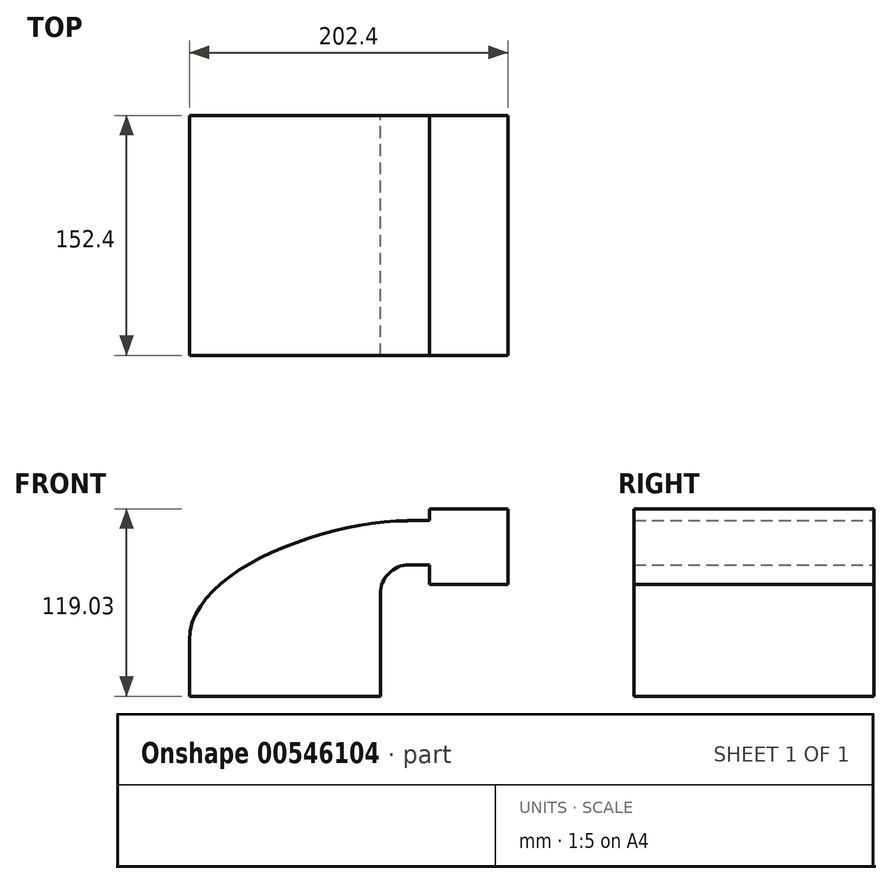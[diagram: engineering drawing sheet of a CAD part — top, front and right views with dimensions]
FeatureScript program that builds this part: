
annotation { "Feature Type Name" : "Feature", "Feature Type Description" : "" }
export const myFeature = defineFeature(function(context is Context, id is Id, definition is map)
    precondition{}
    {
        {
            var Q0;
            Q0=qCreatedBy(makeId("Front.planeOp"),FACE);
            var sketch = newSketch(context, id + "F0", { "sketchPlane" : qUnion([Q0])});
            skLineSegment(sketch, "E0.bottom", {"start": v(-60.63, 17.83) * mm, "end": v(60.63, 17.83) * mm});
            skLineSegment(sketch, "E0.top", {"start": v(-60.63, -17.83) * mm, "end": v(60.63, -17.83) * mm});
            skLineSegment(sketch, "E0.left", {"start": v(-60.63, 17.83) * mm, "end": v(-60.63, -17.83) * mm});
            skLineSegment(sketch, "E0.right", {"start": v(60.63, 17.83) * mm, "end": v(60.63, -17.83) * mm});
            skPoint(sketch, "E0.middle", {"position": v(0, 0) * mm});
            skLineSegment(sketch, "E1.bottom", {"start": v(141.77, 53.05) * mm, "end": v(91.84, 53.05) * mm});
            skLineSegment(sketch, "E1.top", {"start": v(141.77, 101.2) * mm, "end": v(91.84, 101.2) * mm});
            skLineSegment(sketch, "E1.left", {"start": v(141.77, 53.05) * mm, "end": v(141.77, 101.2) * mm});
            skLineSegment(sketch, "E1.right", {"start": v(91.84, 53.05) * mm, "end": v(91.84, 101.2) * mm});
            skPoint(sketch, "E1.middle", {"position": v(116.8, 77.13) * mm});
            skLineSegment(sketch, "E2", {"start": v(60.63, 17.83) * mm, "end": v(60.63, 47.26) * mm});
            skArc(sketch, "E3", {"start": v(60.63, 47.26) * mm, "mid": v(65.99, 60.19) * mm, "end": v(78.92, 65.54) * mm});
            skLineSegment(sketch, "E4", {"start": v(78.92, 65.54) * mm, "end": v(115.89, 65.54) * mm});
            skLineSegment(sketch, "E5.0", {"start": v(78.92, 93.63) * mm, "end": v(115.89, 93.63) * mm});
            skArc(sketch, "E5.1", {"start": v(32.55, 47.26) * mm, "mid": v(46.13, 80.05) * mm, "end": v(78.92, 93.63) * mm});
            skLineSegment(sketch, "E5.2", {"start": v(32.55, 17.83) * mm, "end": v(32.55, 47.26) * mm});
            skLineSegment(sketch, "E6", {"start": v(116.8, 53.05) * mm, "end": v(115.89, 101.2) * mm});
            skFitSpline(sketch, "E7", {"points": [v(-60.63, 17.83) * mm, v(78.92, 93.63) * mm], "startDerivative": vector(0, 131.07) * mm, "endDerivative": vector(165.86, 1.35) * mm});
            skSolve(sketch);
        }
        {
            var Q0;
            Q0=makeQuery(id+"F0.imprint","IMPRINT",FACE,{"disambiguationData":[TD([[makeQuery(id+"F0.imprint","IMPRINT",EDGE,{"derivedFrom":sQuery(id+"F0.wireOp",EDGE,"E0.top")}),1.0]])]});
            var Q1;
            {var subQ3=sQuery(id+"F0.wireOp",EDGE,"E5.2");Q1=makeQuery(id+"F0.imprint","IMPRINT",FACE,{"disambiguationData":[TD([[makeQuery(id+"F0.imprint","IMPRINT",EDGE,{"derivedFrom":subQ3}),1.0]])]});}
            var Q2;
            {var subQ1=sQuery(id+"F0.wireOp",EDGE,"E2");Q2=makeQuery(id+"F0.imprint","IMPRINT",FACE,{"disambiguationData":[TD([[makeQuery(id+"F0.imprint","IMPRINT",EDGE,{"derivedFrom":subQ1}),1.0]])]});}
            var Q3;
            {var subQ6=sQuery(id+"F0.wireOp",EDGE,"E6");Q3=makeQuery(id+"F0.imprint","IMPRINT",FACE,{"disambiguationData":[TD([[makeQuery(id+"F0.imprint","IMPRINT",EDGE,{"derivedFrom":subQ6}),1.0]])]});}
            var Q4;
            {var subQ0=sQuery(id+"F0.wireOp",EDGE,"E1.left");Q4=makeQuery(id+"F0.imprint","IMPRINT",FACE,{"disambiguationData":[TD([[makeQuery(id+"F0.imprint","IMPRINT",EDGE,{"derivedFrom":subQ0}),1.0]])]});}
            extrude(context, id + "F1", {"entities" : qUnion([Q0, Q1, Q2, Q3, Q4]), "endBound" : BoundingType.SYMMETRIC, "depth" : 127 * mm, "offsetDistance" : 25.4 * mm});
        }
        {
            var Q0;
            Q0=makeQuery(id+"F1.opExtrude","CAP_FACE",FACE,{"disambiguationData":[OSD([sQuery(id+"F0.wireOp",EDGE,"E0.top"),sQuery(id+"F0.wireOp",EDGE,"E0.left"),sQuery(id+"F0.wireOp",EDGE,"E0.right"),sQuery(id+"F0.wireOp",EDGE,"E1.bottom"),sQuery(id+"F0.wireOp",EDGE,"E1.top"),sQuery(id+"F0.wireOp",EDGE,"E1.left"),sQuery(id+"F0.wireOp",EDGE,"E1.right"),sQuery(id+"F0.wireOp",EDGE,"E2"),sQuery(id+"F0.wireOp",EDGE,"E3"),sQuery(id+"F0.wireOp",EDGE,"E4"),sQuery(id+"F0.wireOp",EDGE,"E5.0"),sQuery(id+"F0.wireOp",EDGE,"E7")])],"isStart":false});
            extrude(context, id + "F2", {"entities" : qUnion([Q0]), "operationType" : NewBodyOperationType.ADD, "depth" : 25.4 * mm, "offsetDistance" : 25.4 * mm});
        }
    });
